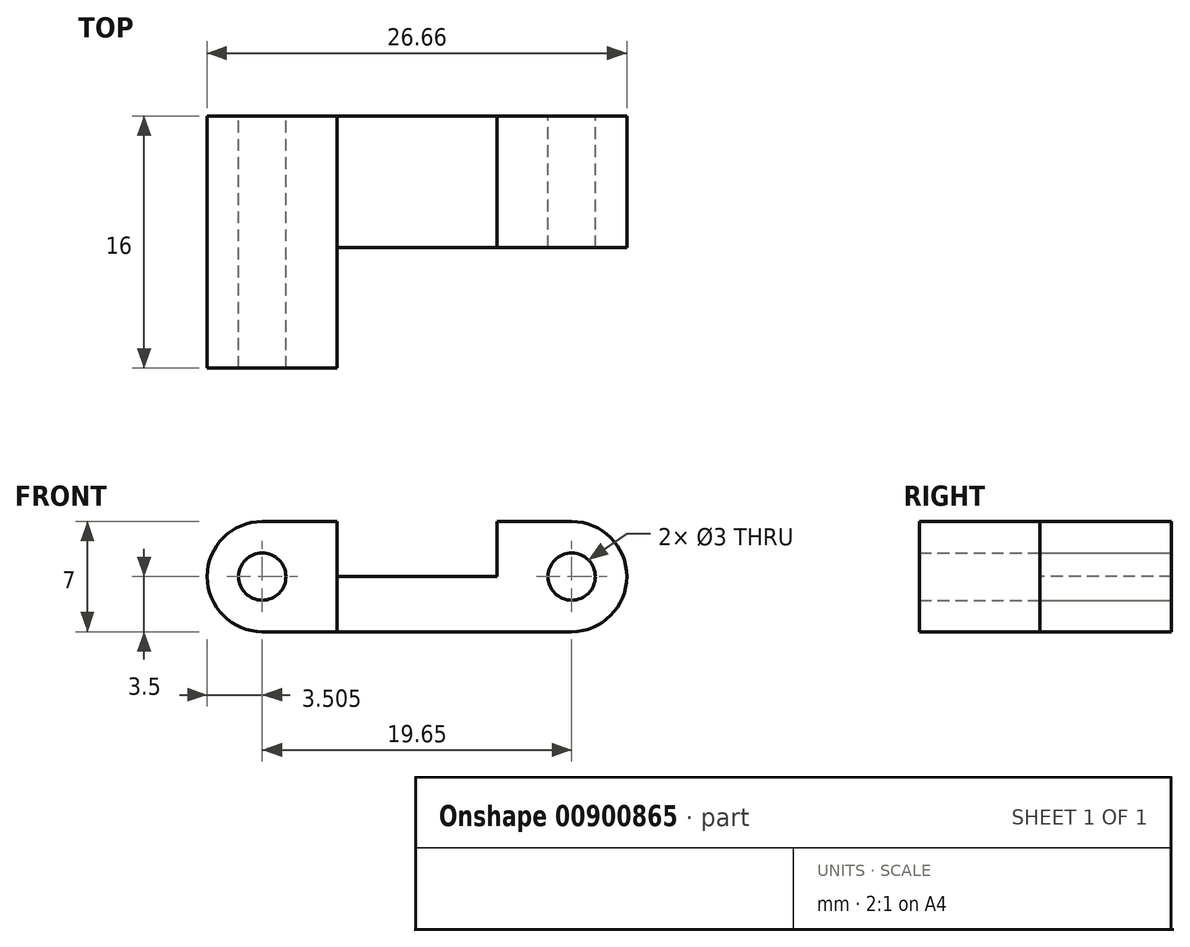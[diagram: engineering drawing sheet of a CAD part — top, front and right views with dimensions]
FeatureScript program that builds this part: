
annotation { "Feature Type Name" : "Feature", "Feature Type Description" : "" }
export const myFeature = defineFeature(function(context is Context, id is Id, definition is map)
    precondition{}
    {
        {
            var Q0;
            Q0=qCreatedBy(makeId("Front.planeOp"),FACE);
            var sketch = newSketch(context, id + "F0", { "sketchPlane" : qUnion([Q0])});
            skArc(sketch, "E0", {"start": v(-9.82, 3.5) * mm, "mid": v(-13.32, 0) * mm, "end": v(-9.82, -3.5) * mm});
            skArc(sketch, "E1", {"start": v(9.82, -3.5) * mm, "mid": v(13.32, 0) * mm, "end": v(9.82, 3.5) * mm});
            skLineSegment(sketch, "E2", {"start": v(-9.82, 3.5) * mm, "end": v(9.82, 3.5) * mm});
            skLineSegment(sketch, "E3", {"start": v(-9.82, -3.5) * mm, "end": v(9.82, -3.5) * mm});
            skCircle(sketch, "E4", {"center": v(-9.82, 0) * mm, "radius": 1.5 * mm});
            skCircle(sketch, "E5", {"center": v(9.82, 0) * mm, "radius": 1.5 * mm});
            skSolve(sketch);
        }
        {
            var Q0;
            Q0 = qSketchRegion(id + "F0", true);
            extrude(context, id + "F1", {"entities" : qUnion([Q0]), "endBound" : BoundingType.SYMMETRIC, "depth" : 16 * mm, "offsetDistance" : 25 * mm});
        }
        {
            var Q0;
            Q0=makeQuery(id+"F1.opExtrude","SWEPT_FACE",FACE,{"disambiguationData":[OSD([sQuery(id+"F0.wireOp",EDGE,"E2")])]});
            var sketch = newSketch(context, id + "F2", { "sketchPlane" : qUnion([Q0])});
            skLineSegment(sketch, "E6.bottom", {"start": v(-5.08, -0.35) * mm, "end": v(27.11, -0.35) * mm});
            skLineSegment(sketch, "E6.top", {"start": v(-5.08, -17.68) * mm, "end": v(27.11, -17.68) * mm});
            skLineSegment(sketch, "E6.left", {"start": v(-5.08, -0.35) * mm, "end": v(-5.08, -17.68) * mm});
            skLineSegment(sketch, "E6.right", {"start": v(27.11, -0.35) * mm, "end": v(27.11, -17.68) * mm});
            skSolve(sketch);
        }
        {
            var Q0;
            {var subQ2=sQuery(id+"F2.wireOp",EDGE,"E6.top");Q0=makeQuery(id+"F2.imprint","IMPRINT",FACE,{"disambiguationData":[TD([[makeQuery(id+"F2.imprint","IMPRINT",EDGE,{"derivedFrom":subQ2}),1.0]])]});}
            var Q1;
            {var subQ0=sQuery(id+"F2.wireOp",EDGE,"E6.left");var subQ1=sQuery(id+"F2.wireOp",EDGE,"E6.bottom");var subQ2=makeQuery(id+"F2.imprint","INTERSECT",VERTEX,{"derivedFrom":[subQ1,subQ0]});Q1=makeQuery(id+"F2.imprint","IMPRINT",FACE,{"disambiguationData":[TD([[makeQuery(id+"F2.imprint","IMPRINT",EDGE,{"disambiguationData":[TD([[subQ2,-1.0]])],"derivedFrom":subQ0}),1.0]])]});}
            extrude(context, id + "F3", {"entities" : qUnion([Q0, Q1]), "operationType" : NewBodyOperationType.REMOVE, "endBound" : BoundingType.THROUGH_ALL, "oppositeDirection" : true, "depth" : 25 * mm, "offsetDistance" : 25 * mm});
        }
        {
            var Q0;
            Q0=makeQuery(id+"F3.boolean.opBoolean","COPY",FACE,{"derivedFrom":makeQuery(id+"F3.opExtrude","SWEPT_FACE",FACE,{"disambiguationData":[OSD([sQuery(id+"F2.wireOp",EDGE,"E6.bottom")])]})});
            var sketch = newSketch(context, id + "F4", { "sketchPlane" : qUnion([Q0])});
            skLineSegment(sketch, "E7.bottom", {"start": v(-5.08, 0) * mm, "end": v(5.08, 0) * mm});
            skLineSegment(sketch, "E7.top", {"start": v(-5.08, 12.1) * mm, "end": v(5.08, 12.1) * mm});
            skLineSegment(sketch, "E7.left", {"start": v(-5.08, 0) * mm, "end": v(-5.08, 12.1) * mm});
            skLineSegment(sketch, "E7.right", {"start": v(5.08, 0) * mm, "end": v(5.08, 12.1) * mm});
            skSolve(sketch);
        }
        {
            var Q0;
            Q0 = qSketchRegion(id + "F4", true);
            extrude(context, id + "F5", {"entities" : qUnion([Q0]), "operationType" : NewBodyOperationType.REMOVE, "endBound" : BoundingType.THROUGH_ALL, "oppositeDirection" : true, "depth" : 25 * mm, "offsetDistance" : 25 * mm});
        }
    });
